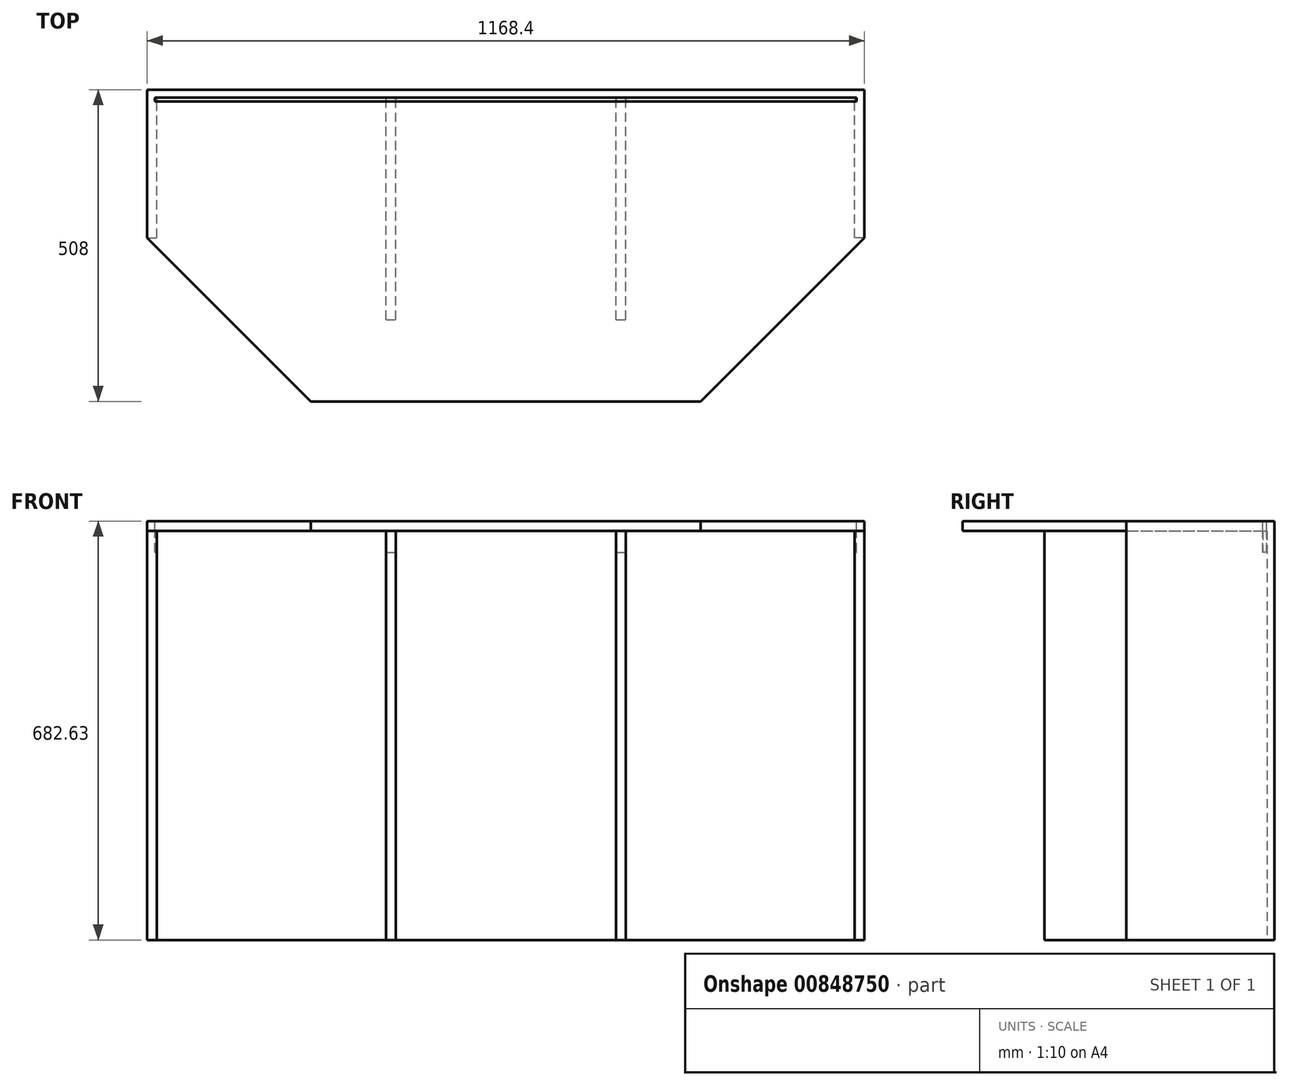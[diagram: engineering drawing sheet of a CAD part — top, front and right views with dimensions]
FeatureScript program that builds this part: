
annotation { "Feature Type Name" : "Feature", "Feature Type Description" : "" }
export const myFeature = defineFeature(function(context is Context, id is Id, definition is map)
    precondition{}
    {
        {
            var Q0;
            Q0=qCreatedBy(makeId("Top.planeOp"),FACE);
            var sketch = newSketch(context, id + "F0", { "sketchPlane" : qUnion([Q0])});
            skLineSegment(sketch, "E0", {"start": v(-584.2, 254) * mm, "end": v(584.2, 254) * mm});
            skLineSegment(sketch, "E1", {"start": v(584.2, 254) * mm, "end": v(584.2, 12.7) * mm});
            skLineSegment(sketch, "E2", {"start": v(-584.2, 254) * mm, "end": v(-584.2, 12.7) * mm});
            skLineSegment(sketch, "E3", {"start": v(-317.5, -254) * mm, "end": v(317.5, -254) * mm});
            skLineSegment(sketch, "E4", {"start": v(584.2, 12.7) * mm, "end": v(317.5, -254) * mm});
            skLineSegment(sketch, "E5", {"start": v(-584.2, 12.7) * mm, "end": v(-317.5, -254) * mm});
            skSolve(sketch);
        }
        {
            var Q0;
            Q0=qSketchRegion(id+"F0",true);
            extrude(context, id + "F1", {"entities" : qUnion([Q0]), "depth" : 15.88 * mm, "offsetDistance" : 25.4 * mm});
        }
        {
            var Q0;
            Q0=makeQuery(id+"F1.opExtrude","CAP_FACE",FACE,{"disambiguationData":[OSD([sQuery(id+"F0.wireOp",EDGE,"E0"),sQuery(id+"F0.wireOp",EDGE,"E1"),sQuery(id+"F0.wireOp",EDGE,"E2"),sQuery(id+"F0.wireOp",EDGE,"E3"),sQuery(id+"F0.wireOp",EDGE,"E4"),sQuery(id+"F0.wireOp",EDGE,"E5")])],"isStart":true});
            var sketch = newSketch(context, id + "F2", { "sketchPlane" : qUnion([Q0])});
            skLineSegment(sketch, "E6.bottom", {"start": v(-584.2, -12.7) * mm, "end": v(-568.33, -12.7) * mm});
            skLineSegment(sketch, "E6.top", {"start": v(-584.2, -254) * mm, "end": v(-568.33, -254) * mm});
            skLineSegment(sketch, "E6.left", {"start": v(-584.2, -12.7) * mm, "end": v(-584.2, -254) * mm});
            skLineSegment(sketch, "E6.right", {"start": v(-568.33, -12.7) * mm, "end": v(-568.33, -238.13) * mm});
            skLineSegment(sketch, "E7.bottom", {"start": v(584.2, -12.7) * mm, "end": v(568.33, -12.7) * mm});
            skLineSegment(sketch, "E7.top", {"start": v(584.2, -254) * mm, "end": v(568.33, -254) * mm});
            skLineSegment(sketch, "E7.left", {"start": v(584.2, -12.7) * mm, "end": v(584.2, -254) * mm});
            skLineSegment(sketch, "E7.right", {"start": v(568.33, -12.7) * mm, "end": v(568.33, -238.12) * mm});
            skLineSegment(sketch, "E8", {"start": v(-568.33, -254) * mm, "end": v(568.33, -254) * mm});
            skLineSegment(sketch, "E9", {"start": v(568.33, -238.12) * mm, "end": v(-568.33, -238.13) * mm});
            skLineSegment(sketch, "E10", {"start": v(-187.32, -238.13) * mm, "end": v(-187.33, 120.65) * mm, "construction": true});
            skLineSegment(sketch, "E11", {"start": v(187.32, -238.12) * mm, "end": v(187.32, 120.65) * mm, "construction": true});
            skLineSegment(sketch, "E12", {"start": v(187.32, 120.65) * mm, "end": v(195.26, 120.65) * mm});
            skLineSegment(sketch, "E13", {"start": v(187.32, 120.65) * mm, "end": v(179.39, 120.65) * mm});
            skLineSegment(sketch, "E14", {"start": v(-187.33, 120.65) * mm, "end": v(-195.26, 120.65) * mm});
            skLineSegment(sketch, "E15", {"start": v(-187.33, 120.65) * mm, "end": v(-179.39, 120.65) * mm});
            skLineSegment(sketch, "E16", {"start": v(195.26, 120.65) * mm, "end": v(195.26, -238.12) * mm});
            skLineSegment(sketch, "E17", {"start": v(179.39, 120.65) * mm, "end": v(179.39, -238.12) * mm});
            skLineSegment(sketch, "E18", {"start": v(-195.26, 120.65) * mm, "end": v(-195.26, -238.13) * mm});
            skLineSegment(sketch, "E19", {"start": v(-179.39, 120.65) * mm, "end": v(-179.39, -238.13) * mm});
            skLineSegment(sketch, "E20", {"start": v(-450.85, 120.65) * mm, "end": v(450.85, 120.65) * mm, "construction": true});
            skSolve(sketch);
        }
        {
            var Q0;
            Q0=qSketchRegion(id+"F2",true);
            extrude(context, id + "F3", {"entities" : qUnion([Q0]), "operationType" : NewBodyOperationType.ADD, "depth" : 666.75 * mm, "offsetDistance" : 25.4 * mm});
        }
        {
            var Q0;
            {var subQ0=sQuery(id+"F2.wireOp",EDGE,"E9");Q0=makeQuery(id+"F3.opExtrude","SWEPT_FACE",FACE,{"disambiguationData":[OSD([subQ0]),TDD([makeQuery(id+"F2.imprint","IMPRINT",EDGE,{"disambiguationData":[TD([[makeQuery(id+"F2.imprint","INTERSECT",VERTEX,{"derivedFrom":[sQuery(id+"F2.wireOp",EDGE,"E6.right"),subQ0]}),1.0]])],"derivedFrom":subQ0})])]});}
            var sketch = newSketch(context, id + "F4", { "sketchPlane" : qUnion([Q0])});
            skLineSegment(sketch, "E21.bottom", {"start": v(-568.33, -666.75) * mm, "end": v(-195.26, -666.75) * mm});
            skLineSegment(sketch, "E21.top", {"start": v(-568.33, -361.95) * mm, "end": v(-195.26, -361.95) * mm});
            skLineSegment(sketch, "E21.left", {"start": v(-568.33, -666.75) * mm, "end": v(-568.33, -361.95) * mm});
            skLineSegment(sketch, "E21.right", {"start": v(-195.26, -666.75) * mm, "end": v(-195.26, -361.95) * mm});
            skLineSegment(sketch, "E22.bottom", {"start": v(-568.33, -358.78) * mm, "end": v(-195.26, -358.78) * mm});
            skLineSegment(sketch, "E22.top", {"start": v(-568.33, -53.98) * mm, "end": v(-195.26, -53.98) * mm});
            skLineSegment(sketch, "E22.left", {"start": v(-568.33, -358.78) * mm, "end": v(-568.33, -53.98) * mm});
            skLineSegment(sketch, "E22.right", {"start": v(-195.26, -358.78) * mm, "end": v(-195.26, -53.97) * mm});
            skLineSegment(sketch, "E23.bottom", {"start": v(-568.33, 0) * mm, "end": v(-195.26, 0) * mm});
            skLineSegment(sketch, "E23.top", {"start": v(-568.33, -50.8) * mm, "end": v(-195.26, -50.8) * mm});
            skLineSegment(sketch, "E23.left", {"start": v(-568.33, 0) * mm, "end": v(-568.33, -50.8) * mm});
            skLineSegment(sketch, "E23.right", {"start": v(-195.26, 0) * mm, "end": v(-195.26, -50.8) * mm});
            skSolve(sketch);
        }
        {
            var Q0;
            Q0=qSketchRegion(id+"F4",true);
            extrude(context, id + "F5", {"entities" : qUnion([Q0]), "operationType" : NewBodyOperationType.ADD, "depth" : 225.3 * mm, "offsetDistance" : 25.4 * mm});
        }
        {
            var Q0;
            {var subQ0=sQuery(id+"F2.wireOp",EDGE,"E9");Q0=makeQuery(id+"F3.opExtrude","SWEPT_FACE",FACE,{"disambiguationData":[OSD([subQ0]),TDD([makeQuery(id+"F2.imprint","IMPRINT",EDGE,{"disambiguationData":[TD([[makeQuery(id+"F2.imprint","INTERSECT",VERTEX,{"derivedFrom":[sQuery(id+"F2.wireOp",EDGE,"E7.right"),subQ0]}),-1.0]])],"derivedFrom":subQ0})])]});}
            var sketch = newSketch(context, id + "F6", { "sketchPlane" : qUnion([Q0])});
            skLineSegment(sketch, "E24.bottom", {"start": v(195.26, -666.75) * mm, "end": v(568.33, -666.75) * mm});
            skLineSegment(sketch, "E24.top", {"start": v(195.26, -361.95) * mm, "end": v(568.33, -361.95) * mm});
            skLineSegment(sketch, "E24.left", {"start": v(195.26, -666.75) * mm, "end": v(195.26, -361.95) * mm});
            skLineSegment(sketch, "E24.right", {"start": v(568.33, -666.75) * mm, "end": v(568.33, -361.95) * mm});
            skLineSegment(sketch, "E25.bottom", {"start": v(195.26, -358.78) * mm, "end": v(568.33, -358.78) * mm});
            skLineSegment(sketch, "E25.top", {"start": v(195.26, -53.98) * mm, "end": v(568.33, -53.98) * mm});
            skLineSegment(sketch, "E25.left", {"start": v(195.26, -358.78) * mm, "end": v(195.26, -53.98) * mm});
            skLineSegment(sketch, "E25.right", {"start": v(568.33, -358.78) * mm, "end": v(568.33, -53.97) * mm});
            skLineSegment(sketch, "E26.bottom", {"start": v(195.26, 0) * mm, "end": v(568.33, 0) * mm});
            skLineSegment(sketch, "E26.top", {"start": v(195.26, -50.8) * mm, "end": v(568.33, -50.8) * mm});
            skLineSegment(sketch, "E26.left", {"start": v(195.26, 0) * mm, "end": v(195.26, -50.8) * mm});
            skLineSegment(sketch, "E26.right", {"start": v(568.33, 0) * mm, "end": v(568.33, -50.8) * mm});
            skSolve(sketch);
        }
        {
            var Q0;
            Q0=qSketchRegion(id+"F6",true);
            extrude(context, id + "F7", {"entities" : qUnion([Q0]), "operationType" : NewBodyOperationType.ADD, "depth" : 225.3 * mm, "offsetDistance" : 25.4 * mm});
        }
        {
            var Q0;
            {var subQ0=sQuery(id+"F2.wireOp",EDGE,"E9");Q0=makeQuery(id+"F3.opExtrude","SWEPT_FACE",FACE,{"disambiguationData":[OSD([subQ0]),TDD([makeQuery(id+"F2.imprint","IMPRINT",EDGE,{"disambiguationData":[TD([[makeQuery(id+"F2.imprint","INTERSECT",VERTEX,{"derivedFrom":[subQ0,sQuery(id+"F2.wireOp",EDGE,"E17")]}),-1.0]])],"derivedFrom":subQ0})])]});}
            var sketch = newSketch(context, id + "F8", { "sketchPlane" : qUnion([Q0])});
            skLineSegment(sketch, "E27.bottom", {"start": v(-179.39, -666.75) * mm, "end": v(179.39, -666.75) * mm});
            skLineSegment(sketch, "E27.top", {"start": v(-179.39, -361.95) * mm, "end": v(179.39, -361.95) * mm});
            skLineSegment(sketch, "E27.left", {"start": v(-179.39, -666.75) * mm, "end": v(-179.39, -361.95) * mm});
            skLineSegment(sketch, "E27.right", {"start": v(179.39, -666.75) * mm, "end": v(179.39, -361.95) * mm});
            skLineSegment(sketch, "E28.bottom", {"start": v(-179.39, -358.78) * mm, "end": v(179.39, -358.78) * mm});
            skLineSegment(sketch, "E28.top", {"start": v(-179.39, -53.98) * mm, "end": v(179.39, -53.98) * mm});
            skLineSegment(sketch, "E28.left", {"start": v(-179.39, -358.78) * mm, "end": v(-179.39, -53.98) * mm});
            skLineSegment(sketch, "E28.right", {"start": v(179.39, -358.78) * mm, "end": v(179.39, -53.97) * mm});
            skLineSegment(sketch, "E29.bottom", {"start": v(-179.39, 0) * mm, "end": v(179.39, 0) * mm});
            skLineSegment(sketch, "E29.top", {"start": v(-179.39, -50.8) * mm, "end": v(179.39, -50.8) * mm});
            skLineSegment(sketch, "E29.left", {"start": v(-179.39, 0) * mm, "end": v(-179.39, -50.8) * mm});
            skLineSegment(sketch, "E29.right", {"start": v(179.39, 0) * mm, "end": v(179.39, -50.8) * mm});
            skSolve(sketch);
        }
        {
            var Q0;
            Q0=qSketchRegion(id+"F8",true);
            extrude(context, id + "F9", {"entities" : qUnion([Q0]), "operationType" : NewBodyOperationType.ADD, "depth" : 358.65 * mm, "offsetDistance" : 25.4 * mm});
        }
        {
            var Q0;
            Q0=makeQuery(id+"F5.opExtrude","CAP_FACE",FACE,{"disambiguationData":[OSD([sQuery(id+"F4.wireOp",EDGE,"E21.bottom"),sQuery(id+"F4.wireOp",EDGE,"E21.top"),sQuery(id+"F4.wireOp",EDGE,"E21.left"),sQuery(id+"F4.wireOp",EDGE,"E21.right")])],"isStart":false});
            var sketch = newSketch(context, id + "F10", { "sketchPlane" : qUnion([Q0])});
            skLineSegment(sketch, "E30", {"start": v(-381.8, -361.95) * mm, "end": v(-381.8, -666.75) * mm, "construction": true});
            skLineSegment(sketch, "E31", {"start": v(-195.26, -514.35) * mm, "end": v(-568.33, -514.35) * mm, "construction": true});
            skCircle(sketch, "E32", {"center": v(-381.8, -514.35) * mm, "radius": 12.7 * mm});
            skSolve(sketch);
        }
        {
            var Q0;
            Q0=qSketchRegion(id+"F10",true);
            extrude(context, id + "F11", {"entities" : qUnion([Q0]), "operationType" : NewBodyOperationType.ADD, "depth" : 25.4 * mm, "offsetDistance" : 25.4 * mm});
        }
        {
            var Q0;
            Q0=makeQuery(id+"F5.opExtrude","CAP_FACE",FACE,{"disambiguationData":[OSD([sQuery(id+"F4.wireOp",EDGE,"E22.bottom"),sQuery(id+"F4.wireOp",EDGE,"E22.top"),sQuery(id+"F4.wireOp",EDGE,"E22.left"),sQuery(id+"F4.wireOp",EDGE,"E22.right")])],"isStart":false});
            var sketch = newSketch(context, id + "F12", { "sketchPlane" : qUnion([Q0])});
            skLineSegment(sketch, "E33", {"start": v(-568.33, -206.38) * mm, "end": v(-195.26, -206.38) * mm, "construction": true});
            skLineSegment(sketch, "E34", {"start": v(-381.8, -53.98) * mm, "end": v(-381.8, -358.78) * mm, "construction": true});
            skCircle(sketch, "E35", {"center": v(-381.8, -206.38) * mm, "radius": 12.7 * mm});
            skSolve(sketch);
        }
        {
            var Q0;
            Q0=qSketchRegion(id+"F12",true);
            extrude(context, id + "F13", {"entities" : qUnion([Q0]), "operationType" : NewBodyOperationType.ADD, "depth" : 25.4 * mm, "offsetDistance" : 25.4 * mm});
        }
        {
            var Q0;
            Q0=makeQuery(id+"F5.opExtrude","CAP_FACE",FACE,{"disambiguationData":[OSD([sQuery(id+"F4.wireOp",EDGE,"E23.bottom"),sQuery(id+"F4.wireOp",EDGE,"E23.top"),sQuery(id+"F4.wireOp",EDGE,"E23.left"),sQuery(id+"F4.wireOp",EDGE,"E23.right")])],"isStart":false});
            var sketch = newSketch(context, id + "F14", { "sketchPlane" : qUnion([Q0])});
            skLineSegment(sketch, "E36", {"start": v(-568.33, -25.4) * mm, "end": v(-195.26, -25.4) * mm, "construction": true});
            skLineSegment(sketch, "E37", {"start": v(-381.8, -50.8) * mm, "end": v(-381.8, 0) * mm, "construction": true});
            skCircle(sketch, "E38", {"center": v(-381.8, -25.4) * mm, "radius": 12.7 * mm});
            skSolve(sketch);
        }
        {
            var Q0;
            Q0=qSketchRegion(id+"F14",true);
            extrude(context, id + "F15", {"entities" : qUnion([Q0]), "operationType" : NewBodyOperationType.ADD, "depth" : 25.4 * mm, "offsetDistance" : 25.4 * mm});
        }
        {
            var Q0;
            Q0=makeQuery(id+"F9.opExtrude","CAP_FACE",FACE,{"disambiguationData":[OSD([sQuery(id+"F8.wireOp",EDGE,"E27.bottom"),sQuery(id+"F8.wireOp",EDGE,"E27.top"),sQuery(id+"F8.wireOp",EDGE,"E27.left"),sQuery(id+"F8.wireOp",EDGE,"E27.right")])],"isStart":false});
            var sketch = newSketch(context, id + "F16", { "sketchPlane" : qUnion([Q0])});
            skLineSegment(sketch, "E39", {"start": v(-179.39, -514.35) * mm, "end": v(179.39, -514.35) * mm, "construction": true});
            skLineSegment(sketch, "E40", {"start": v(0, -361.95) * mm, "end": v(0, -666.75) * mm, "construction": true});
            skCircle(sketch, "E41", {"center": v(0, -514.35) * mm, "radius": 12.7 * mm});
            skSolve(sketch);
        }
        {
            var Q0;
            Q0=qSketchRegion(id+"F16",true);
            extrude(context, id + "F17", {"entities" : qUnion([Q0]), "operationType" : NewBodyOperationType.ADD, "depth" : 25.4 * mm, "offsetDistance" : 25.4 * mm});
        }
        {
            var Q0;
            Q0=makeQuery(id+"F9.opExtrude","CAP_FACE",FACE,{"disambiguationData":[OSD([sQuery(id+"F8.wireOp",EDGE,"E28.bottom"),sQuery(id+"F8.wireOp",EDGE,"E28.top"),sQuery(id+"F8.wireOp",EDGE,"E28.left"),sQuery(id+"F8.wireOp",EDGE,"E28.right")])],"isStart":false});
            var sketch = newSketch(context, id + "F18", { "sketchPlane" : qUnion([Q0])});
            skLineSegment(sketch, "E42", {"start": v(-179.39, -206.38) * mm, "end": v(179.39, -206.38) * mm, "construction": true});
            skLineSegment(sketch, "E43", {"start": v(0, -53.98) * mm, "end": v(0, -358.78) * mm, "construction": true});
            skCircle(sketch, "E44", {"center": v(0, -206.38) * mm, "radius": 12.7 * mm});
            skSolve(sketch);
        }
        {
            var Q0;
            Q0=qSketchRegion(id+"F18",true);
            extrude(context, id + "F19", {"entities" : qUnion([Q0]), "operationType" : NewBodyOperationType.ADD, "depth" : 25.4 * mm, "offsetDistance" : 25.4 * mm});
        }
        {
            var Q0;
            Q0=makeQuery(id+"F9.opExtrude","CAP_FACE",FACE,{"disambiguationData":[OSD([sQuery(id+"F8.wireOp",EDGE,"E29.bottom"),sQuery(id+"F8.wireOp",EDGE,"E29.top"),sQuery(id+"F8.wireOp",EDGE,"E29.left"),sQuery(id+"F8.wireOp",EDGE,"E29.right")])],"isStart":false});
            var sketch = newSketch(context, id + "F20", { "sketchPlane" : qUnion([Q0])});
            skLineSegment(sketch, "E45", {"start": v(179.39, -25.4) * mm, "end": v(-179.39, -25.4) * mm, "construction": true});
            skLineSegment(sketch, "E46", {"start": v(0, -50.8) * mm, "end": v(0, 0) * mm, "construction": true});
            skCircle(sketch, "E47", {"center": v(0, -25.4) * mm, "radius": 12.7 * mm});
            skSolve(sketch);
        }
        {
            var Q0;
            Q0=qSketchRegion(id+"F20",true);
            extrude(context, id + "F21", {"entities" : qUnion([Q0]), "operationType" : NewBodyOperationType.ADD, "depth" : 25.4 * mm, "offsetDistance" : 25.4 * mm});
        }
        {
            var Q0;
            Q0=makeQuery(id+"F7.opExtrude","CAP_FACE",FACE,{"disambiguationData":[OSD([sQuery(id+"F6.wireOp",EDGE,"E24.bottom"),sQuery(id+"F6.wireOp",EDGE,"E24.top"),sQuery(id+"F6.wireOp",EDGE,"E24.left"),sQuery(id+"F6.wireOp",EDGE,"E24.right")])],"isStart":false});
            var sketch = newSketch(context, id + "F22", { "sketchPlane" : qUnion([Q0])});
            skLineSegment(sketch, "E48", {"start": v(568.33, -514.35) * mm, "end": v(195.26, -514.35) * mm, "construction": true});
            skLineSegment(sketch, "E49", {"start": v(381.8, -361.95) * mm, "end": v(381.8, -666.75) * mm, "construction": true});
            skCircle(sketch, "E50", {"center": v(381.8, -514.35) * mm, "radius": 12.7 * mm});
            skSolve(sketch);
        }
        {
            var Q0;
            Q0=qSketchRegion(id+"F22",true);
            extrude(context, id + "F23", {"entities" : qUnion([Q0]), "operationType" : NewBodyOperationType.ADD, "depth" : 25.4 * mm, "offsetDistance" : 25.4 * mm});
        }
        {
            var Q0;
            Q0=makeQuery(id+"F7.opExtrude","CAP_FACE",FACE,{"disambiguationData":[OSD([sQuery(id+"F6.wireOp",EDGE,"E25.bottom"),sQuery(id+"F6.wireOp",EDGE,"E25.top"),sQuery(id+"F6.wireOp",EDGE,"E25.left"),sQuery(id+"F6.wireOp",EDGE,"E25.right")])],"isStart":false});
            var sketch = newSketch(context, id + "F24", { "sketchPlane" : qUnion([Q0])});
            skLineSegment(sketch, "E51", {"start": v(195.26, -206.38) * mm, "end": v(568.33, -206.38) * mm, "construction": true});
            skLineSegment(sketch, "E52", {"start": v(381.8, -53.98) * mm, "end": v(381.8, -358.78) * mm, "construction": true});
            skCircle(sketch, "E53", {"center": v(381.8, -206.38) * mm, "radius": 12.7 * mm});
            skSolve(sketch);
        }
        {
            var Q0;
            Q0=qSketchRegion(id+"F24",true);
            extrude(context, id + "F25", {"entities" : qUnion([Q0]), "operationType" : NewBodyOperationType.ADD, "depth" : 25.4 * mm, "offsetDistance" : 25.4 * mm});
        }
        {
            var Q0;
            Q0=makeQuery(id+"F7.opExtrude","CAP_FACE",FACE,{"disambiguationData":[OSD([sQuery(id+"F6.wireOp",EDGE,"E26.bottom"),sQuery(id+"F6.wireOp",EDGE,"E26.top"),sQuery(id+"F6.wireOp",EDGE,"E26.left"),sQuery(id+"F6.wireOp",EDGE,"E26.right")])],"isStart":false});
            var sketch = newSketch(context, id + "F26", { "sketchPlane" : qUnion([Q0])});
            skLineSegment(sketch, "E54", {"start": v(568.33, -25.4) * mm, "end": v(195.26, -25.4) * mm, "construction": true});
            skLineSegment(sketch, "E55", {"start": v(381.8, -50.8) * mm, "end": v(381.8, 0) * mm, "construction": true});
            skCircle(sketch, "E56", {"center": v(381.8, -25.4) * mm, "radius": 12.7 * mm});
            skSolve(sketch);
        }
        {
            var Q0;
            Q0=qSketchRegion(id+"F26",true);
            extrude(context, id + "F27", {"entities" : qUnion([Q0]), "operationType" : NewBodyOperationType.ADD, "depth" : 25.4 * mm, "offsetDistance" : 25.4 * mm});
        }
        {
            var Q0;
            {var subQ0=sQuery(id+"F2.wireOp",EDGE,"E17");var subQ2=sQuery(id+"F2.wireOp",EDGE,"E9");Q0=makeQuery(id+"F9.boolean.opBoolean","SPLIT",FACE,{"disambiguationData":[TD([makeQuery(id+"F9.opExtrude","SWEPT_FACE",FACE,{"disambiguationData":[OSD([sQuery(id+"F8.wireOp",EDGE,"E27.top")])]})])],"derivedFrom":makeQuery(id+"F3.opExtrude","SWEPT_FACE",FACE,{"disambiguationData":[OSD([subQ2]),TDD([makeQuery(id+"F2.imprint","IMPRINT",EDGE,{"disambiguationData":[TD([[makeQuery(id+"F2.imprint","INTERSECT",VERTEX,{"derivedFrom":[subQ2,subQ0]}),-1.0]])],"derivedFrom":subQ2})])]})});}
            var sketch = newSketch(context, id + "F28", { "sketchPlane" : qUnion([Q0])});
            skLineSegment(sketch, "E57.0", {"start": v(179.39, -358.78) * mm, "end": v(-179.39, -358.78) * mm});
            skLineSegment(sketch, "E57.1", {"start": v(179.39, -361.95) * mm, "end": v(179.39, -358.78) * mm});
            skLineSegment(sketch, "E57.2", {"start": v(-179.39, -361.95) * mm, "end": v(179.39, -361.95) * mm});
            skLineSegment(sketch, "E57.3", {"start": v(-179.39, -358.78) * mm, "end": v(-179.39, -361.95) * mm});
            skSolve(sketch);
        }
        {
            var Q0;
            Q0=qSketchRegion(id+"F28",true);
            extrude(context, id + "F29", {"entities" : qUnion([Q0]), "operationType" : NewBodyOperationType.ADD, "depth" : 358.77 * mm, "offsetDistance" : 25.4 * mm});
        }
        {
            var Q0;
            {var subQ0=sQuery(id+"F2.wireOp",EDGE,"E17");var subQ2=sQuery(id+"F2.wireOp",EDGE,"E9");Q0=makeQuery(id+"F9.boolean.opBoolean","SPLIT",FACE,{"disambiguationData":[TD([makeQuery(id+"F9.opExtrude","SWEPT_FACE",FACE,{"disambiguationData":[OSD([sQuery(id+"F8.wireOp",EDGE,"E28.top")])]})])],"derivedFrom":makeQuery(id+"F3.opExtrude","SWEPT_FACE",FACE,{"disambiguationData":[OSD([subQ2]),TDD([makeQuery(id+"F2.imprint","IMPRINT",EDGE,{"disambiguationData":[TD([[makeQuery(id+"F2.imprint","INTERSECT",VERTEX,{"derivedFrom":[subQ2,subQ0]}),-1.0]])],"derivedFrom":subQ2})])]})});}
            var sketch = newSketch(context, id + "F30", { "sketchPlane" : qUnion([Q0])});
            skLineSegment(sketch, "E58.0", {"start": v(179.39, -50.8) * mm, "end": v(-179.39, -50.8) * mm});
            skLineSegment(sketch, "E58.1", {"start": v(179.39, -53.97) * mm, "end": v(179.39, -50.8) * mm});
            skLineSegment(sketch, "E58.2", {"start": v(-179.39, -53.98) * mm, "end": v(179.39, -53.98) * mm});
            skLineSegment(sketch, "E58.3", {"start": v(-179.39, -50.8) * mm, "end": v(-179.39, -53.97) * mm});
            skSolve(sketch);
        }
        {
            var Q0;
            Q0=qSketchRegion(id+"F30",true);
            extrude(context, id + "F31", {"entities" : qUnion([Q0]), "operationType" : NewBodyOperationType.ADD, "depth" : 358.77 * mm, "offsetDistance" : 25.4 * mm});
        }
        {
            var Q0;
            {var subQ0=sQuery(id+"F2.wireOp",EDGE,"E6.right");var subQ2=sQuery(id+"F2.wireOp",EDGE,"E9");Q0=makeQuery(id+"F5.boolean.opBoolean","SPLIT",FACE,{"disambiguationData":[TD([makeQuery(id+"F5.opExtrude","SWEPT_FACE",FACE,{"disambiguationData":[OSD([sQuery(id+"F4.wireOp",EDGE,"E21.top")])]})])],"derivedFrom":makeQuery(id+"F3.opExtrude","SWEPT_FACE",FACE,{"disambiguationData":[OSD([subQ2]),TDD([makeQuery(id+"F2.imprint","IMPRINT",EDGE,{"disambiguationData":[TD([[makeQuery(id+"F2.imprint","INTERSECT",VERTEX,{"derivedFrom":[subQ0,subQ2]}),1.0]])],"derivedFrom":subQ2})])]})});}
            var sketch = newSketch(context, id + "F32", { "sketchPlane" : qUnion([Q0])});
            skLineSegment(sketch, "E59.0", {"start": v(-195.26, -358.78) * mm, "end": v(-568.33, -358.78) * mm});
            skLineSegment(sketch, "E59.1", {"start": v(-195.26, -361.95) * mm, "end": v(-195.26, -358.78) * mm});
            skLineSegment(sketch, "E59.2", {"start": v(-568.33, -361.95) * mm, "end": v(-195.26, -361.95) * mm});
            skLineSegment(sketch, "E59.3", {"start": v(-568.33, -358.78) * mm, "end": v(-568.33, -361.95) * mm});
            skSolve(sketch);
        }
        {
            var Q0;
            Q0=qSketchRegion(id+"F32",true);
            extrude(context, id + "F33", {"entities" : qUnion([Q0]), "operationType" : NewBodyOperationType.ADD, "depth" : 225.42 * mm, "offsetDistance" : 25.4 * mm});
        }
        {
            var Q0;
            {var subQ0=sQuery(id+"F2.wireOp",EDGE,"E6.right");var subQ2=sQuery(id+"F2.wireOp",EDGE,"E9");Q0=makeQuery(id+"F5.boolean.opBoolean","SPLIT",FACE,{"disambiguationData":[TD([makeQuery(id+"F5.opExtrude","SWEPT_FACE",FACE,{"disambiguationData":[OSD([sQuery(id+"F4.wireOp",EDGE,"E22.top")])]})])],"derivedFrom":makeQuery(id+"F3.opExtrude","SWEPT_FACE",FACE,{"disambiguationData":[OSD([subQ2]),TDD([makeQuery(id+"F2.imprint","IMPRINT",EDGE,{"disambiguationData":[TD([[makeQuery(id+"F2.imprint","INTERSECT",VERTEX,{"derivedFrom":[subQ0,subQ2]}),1.0]])],"derivedFrom":subQ2})])]})});}
            var sketch = newSketch(context, id + "F34", { "sketchPlane" : qUnion([Q0])});
            skLineSegment(sketch, "E60.0", {"start": v(-195.26, -50.8) * mm, "end": v(-568.33, -50.8) * mm});
            skLineSegment(sketch, "E60.1", {"start": v(-195.26, -53.97) * mm, "end": v(-195.26, -50.8) * mm});
            skLineSegment(sketch, "E60.2", {"start": v(-568.33, -53.98) * mm, "end": v(-195.26, -53.98) * mm});
            skLineSegment(sketch, "E60.3", {"start": v(-568.33, -50.8) * mm, "end": v(-568.33, -53.97) * mm});
            skSolve(sketch);
        }
        {
            var Q0;
            Q0=qSketchRegion(id+"F34",true);
            extrude(context, id + "F35", {"entities" : qUnion([Q0]), "operationType" : NewBodyOperationType.ADD, "depth" : 225.42 * mm, "offsetDistance" : 25.4 * mm});
        }
        {
            var Q0;
            {var subQ0=sQuery(id+"F2.wireOp",EDGE,"E7.right");var subQ2=sQuery(id+"F2.wireOp",EDGE,"E9");Q0=makeQuery(id+"F7.boolean.opBoolean","SPLIT",FACE,{"disambiguationData":[TD([makeQuery(id+"F7.opExtrude","SWEPT_FACE",FACE,{"disambiguationData":[OSD([sQuery(id+"F6.wireOp",EDGE,"E25.top")])]})])],"derivedFrom":makeQuery(id+"F3.opExtrude","SWEPT_FACE",FACE,{"disambiguationData":[OSD([subQ2]),TDD([makeQuery(id+"F2.imprint","IMPRINT",EDGE,{"disambiguationData":[TD([[makeQuery(id+"F2.imprint","INTERSECT",VERTEX,{"derivedFrom":[subQ0,subQ2]}),-1.0]])],"derivedFrom":subQ2})])]})});}
            var sketch = newSketch(context, id + "F36", { "sketchPlane" : qUnion([Q0])});
            skLineSegment(sketch, "E61.0", {"start": v(568.33, -50.8) * mm, "end": v(195.26, -50.8) * mm});
            skLineSegment(sketch, "E61.1", {"start": v(568.33, -53.97) * mm, "end": v(568.33, -50.8) * mm});
            skLineSegment(sketch, "E61.2", {"start": v(195.26, -53.98) * mm, "end": v(568.33, -53.98) * mm});
            skLineSegment(sketch, "E61.3", {"start": v(195.26, -50.8) * mm, "end": v(195.26, -53.97) * mm});
            skSolve(sketch);
        }
        {
            var Q0;
            Q0=qSketchRegion(id+"F36",true);
            extrude(context, id + "F37", {"entities" : qUnion([Q0]), "operationType" : NewBodyOperationType.ADD, "depth" : 225.42 * mm, "offsetDistance" : 25.4 * mm});
        }
        {
            var Q0;
            {var subQ0=sQuery(id+"F2.wireOp",EDGE,"E7.right");var subQ2=sQuery(id+"F2.wireOp",EDGE,"E9");Q0=makeQuery(id+"F7.boolean.opBoolean","SPLIT",FACE,{"disambiguationData":[TD([makeQuery(id+"F7.opExtrude","SWEPT_FACE",FACE,{"disambiguationData":[OSD([sQuery(id+"F6.wireOp",EDGE,"E24.top")])]})])],"derivedFrom":makeQuery(id+"F3.opExtrude","SWEPT_FACE",FACE,{"disambiguationData":[OSD([subQ2]),TDD([makeQuery(id+"F2.imprint","IMPRINT",EDGE,{"disambiguationData":[TD([[makeQuery(id+"F2.imprint","INTERSECT",VERTEX,{"derivedFrom":[subQ0,subQ2]}),-1.0]])],"derivedFrom":subQ2})])]})});}
            var sketch = newSketch(context, id + "F38", { "sketchPlane" : qUnion([Q0])});
            skLineSegment(sketch, "E62.0", {"start": v(568.33, -358.78) * mm, "end": v(195.26, -358.78) * mm});
            skLineSegment(sketch, "E62.1", {"start": v(568.33, -361.95) * mm, "end": v(568.33, -358.78) * mm});
            skLineSegment(sketch, "E62.2", {"start": v(195.26, -361.95) * mm, "end": v(568.33, -361.95) * mm});
            skLineSegment(sketch, "E62.3", {"start": v(195.26, -358.78) * mm, "end": v(195.26, -361.95) * mm});
            skSolve(sketch);
        }
        {
            var Q0;
            Q0=qSketchRegion(id+"F38",true);
            extrude(context, id + "F39", {"entities" : qUnion([Q0]), "operationType" : NewBodyOperationType.ADD, "depth" : 225.42 * mm, "offsetDistance" : 25.4 * mm});
        }
        {
            var Q0;
            Q0=makeQuery(id+"F1.opExtrude","CAP_FACE",FACE,{"disambiguationData":[OSD([sQuery(id+"F0.wireOp",EDGE,"E0"),sQuery(id+"F0.wireOp",EDGE,"E1"),sQuery(id+"F0.wireOp",EDGE,"E2"),sQuery(id+"F0.wireOp",EDGE,"E3"),sQuery(id+"F0.wireOp",EDGE,"E4"),sQuery(id+"F0.wireOp",EDGE,"E5")])],"isStart":false});
            var sketch = newSketch(context, id + "F40", { "sketchPlane" : qUnion([Q0])});
            skLineSegment(sketch, "E63.bottom", {"start": v(-571.5, 241.3) * mm, "end": v(571.5, 241.3) * mm});
            skLineSegment(sketch, "E63.top", {"start": v(-571.5, 234.95) * mm, "end": v(571.5, 234.95) * mm});
            skLineSegment(sketch, "E63.left", {"start": v(-571.5, 241.3) * mm, "end": v(-571.5, 234.95) * mm});
            skLineSegment(sketch, "E63.right", {"start": v(571.5, 241.3) * mm, "end": v(571.5, 234.95) * mm});
            skSolve(sketch);
        }
        {
            var Q0;
            Q0 = qSketchRegion(id + "F40", true);
            extrude(context, id + "F41", {"entities" : qUnion([Q0]), "operationType" : NewBodyOperationType.REMOVE, "oppositeDirection" : true, "depth" : 50.8 * mm, "offsetDistance" : 25.4 * mm});
        }
        {
            var Q0;
            Q0=makeQuery(id+"F5.opExtrude","CAP_FACE",FACE,{"disambiguationData":[OSD([sQuery(id+"F4.wireOp",EDGE,"E23.bottom"),sQuery(id+"F4.wireOp",EDGE,"E23.top"),sQuery(id+"F4.wireOp",EDGE,"E23.left"),sQuery(id+"F4.wireOp",EDGE,"E23.right")])],"isStart":false});
            var sketch = newSketch(context, id + "F42", { "sketchPlane" : qUnion([Q0])});
            skLineSegment(sketch, "E64", {"start": v(-568.33, 0) * mm, "end": v(-568.33, -754) * mm});
            skLineSegment(sketch, "E65", {"start": v(-568.33, 0) * mm, "end": v(-195.26, 0) * mm});
            skLineSegment(sketch, "E66", {"start": v(-195.26, 0) * mm, "end": v(-195.26, -758.52) * mm});
            skLineSegment(sketch, "E67", {"start": v(-195.26, -758.52) * mm, "end": v(-568.33, -754) * mm});
            skSolve(sketch);
        }
        {
            var Q0;
            Q0 = qSketchRegion(id + "F42", true);
            extrude(context, id + "F43", {"entities" : qUnion([Q0]), "operationType" : NewBodyOperationType.REMOVE, "endBound" : BoundingType.SYMMETRIC, "oppositeDirection" : true, "depth" : 457.2 * mm, "offsetDistance" : 25.4 * mm});
        }
        {
            var Q0;
            Q0=makeQuery(id+"F7.opExtrude","CAP_FACE",FACE,{"disambiguationData":[OSD([sQuery(id+"F6.wireOp",EDGE,"E26.bottom"),sQuery(id+"F6.wireOp",EDGE,"E26.top"),sQuery(id+"F6.wireOp",EDGE,"E26.left"),sQuery(id+"F6.wireOp",EDGE,"E26.right")])],"isStart":false});
            var sketch = newSketch(context, id + "F44", { "sketchPlane" : qUnion([Q0])});
            skLineSegment(sketch, "E68", {"start": v(195.26, 0) * mm, "end": v(195.26, -771.91) * mm});
            skLineSegment(sketch, "E69", {"start": v(195.26, 0) * mm, "end": v(568.33, 0) * mm});
            skLineSegment(sketch, "E70", {"start": v(568.33, 0) * mm, "end": v(568.33, -734.96) * mm});
            skLineSegment(sketch, "E71", {"start": v(195.26, -771.91) * mm, "end": v(568.33, -734.96) * mm});
            skSolve(sketch);
        }
        {
            var Q0;
            Q0 = qSketchRegion(id + "F44", true);
            extrude(context, id + "F45", {"entities" : qUnion([Q0]), "operationType" : NewBodyOperationType.REMOVE, "endBound" : BoundingType.SYMMETRIC, "oppositeDirection" : true, "depth" : 457.2 * mm, "offsetDistance" : 25.4 * mm});
        }
        {
            var Q0;
            Q0=makeQuery(id+"F9.opExtrude","CAP_FACE",FACE,{"disambiguationData":[OSD([sQuery(id+"F8.wireOp",EDGE,"E29.bottom"),sQuery(id+"F8.wireOp",EDGE,"E29.top"),sQuery(id+"F8.wireOp",EDGE,"E29.left"),sQuery(id+"F8.wireOp",EDGE,"E29.right")])],"isStart":false});
            var sketch = newSketch(context, id + "F46", { "sketchPlane" : qUnion([Q0])});
            skLineSegment(sketch, "E72", {"start": v(-179.39, 0) * mm, "end": v(-179.39, -746.5) * mm});
            skLineSegment(sketch, "E73", {"start": v(-179.39, 0) * mm, "end": v(179.39, 0) * mm});
            skLineSegment(sketch, "E74", {"start": v(179.39, 0) * mm, "end": v(179.39, -735.2) * mm});
            skLineSegment(sketch, "E75", {"start": v(179.39, -735.2) * mm, "end": v(-179.39, -746.5) * mm});
            skSolve(sketch);
        }
        {
            var Q0;
            Q0 = qSketchRegion(id + "F46", true);
            extrude(context, id + "F47", {"entities" : qUnion([Q0]), "operationType" : NewBodyOperationType.REMOVE, "endBound" : BoundingType.SYMMETRIC, "oppositeDirection" : true, "depth" : 723.9 * mm, "offsetDistance" : 25.4 * mm});
        }
        {
            var Q0;
            Q0=makeQuery(id+"F41.boolean.opBoolean","COPY",FACE,{"derivedFrom":makeQuery(id+"F41.opExtrude","SWEPT_FACE",FACE,{"disambiguationData":[OSD([sQuery(id+"F40.wireOp",EDGE,"E63.bottom")])]})});
            var sketch = newSketch(context, id + "F48", { "sketchPlane" : qUnion([Q0])});
            skLineSegment(sketch, "E76.bottom", {"start": v(-571.5, 15.88) * mm, "end": v(571.5, 15.88) * mm});
            skLineSegment(sketch, "E76.top", {"start": v(-571.5, 0) * mm, "end": v(571.5, 0) * mm});
            skLineSegment(sketch, "E76.left", {"start": v(-571.5, 15.88) * mm, "end": v(-571.5, 0) * mm});
            skLineSegment(sketch, "E77", {"start": v(571.5, 0) * mm, "end": v(571.5, 15.88) * mm});
            skSolve(sketch);
        }
        {
            var Q0;
            Q0 = qSketchRegion(id + "F48", true);
            extrude(context, id + "F49", {"entities" : qUnion([Q0]), "depth" : 6.35 * mm, "offsetDistance" : 25.4 * mm});
        }
    });
